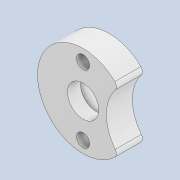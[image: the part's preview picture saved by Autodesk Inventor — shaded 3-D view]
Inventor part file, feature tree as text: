
AUTODESK INVENTOR PART (.ipt)
format: ipt  version: 2020 (Build 240168000, 168)  size: 125,952 bytes
history: native  units: mm
features: sketch x4, extrude x3, other x2, hole x1, fillet x1, reference x1
ambient origin geometry x8: Origin, YZ Plane, XZ Plane, XY Plane, X Axis, Y Axis, Z Axis, Center Point
bodies: Solid1 (feature_tree)
feature tree (12):
  extrude  "Extrusion1"  Depth=35.0mm
  hole  "Hole1"  [1 undecoded]
  extrude  "Extrusion3"  Depth=2.0mm
  extrude  "Extrusion4"  TaperAngle=0.0deg  [1 undecoded]
  fillet  "Fillet1"  Radius=2.0mm
  sketch  "Sketch1"  dims[d0=12.0mm d1=35.0mm]
  sketch  "Sketch4"  dims[d2=10.0mm d3=0.0mm d7=26.0mm]
  sketch  "Sketch5"  dims[d8=5.0mm d9=6.0mm d10=4.0mm d11=2.0mm d12=90.0deg d13=8.0mm d14=20.594885mm d15=16.3mm]
  sketch  "Sketch6"  dims[d16=5.0mm d17=0.0mm d19=0.0mm d20=0.0mm d21=2.0mm d22=1.0mm]
  reference  "Reference2"
  other  "0008-10-10 Injectomat Standard_Seringa 20.iam"
  other  "0008-10-002 Corp_Injectomat1.ipt:10"
note: 2 required parameter values undecoded (feature->parameter linkage not recoverable at this tier; creation-order binding heuristic only, values carry confidence <= 0.55)
